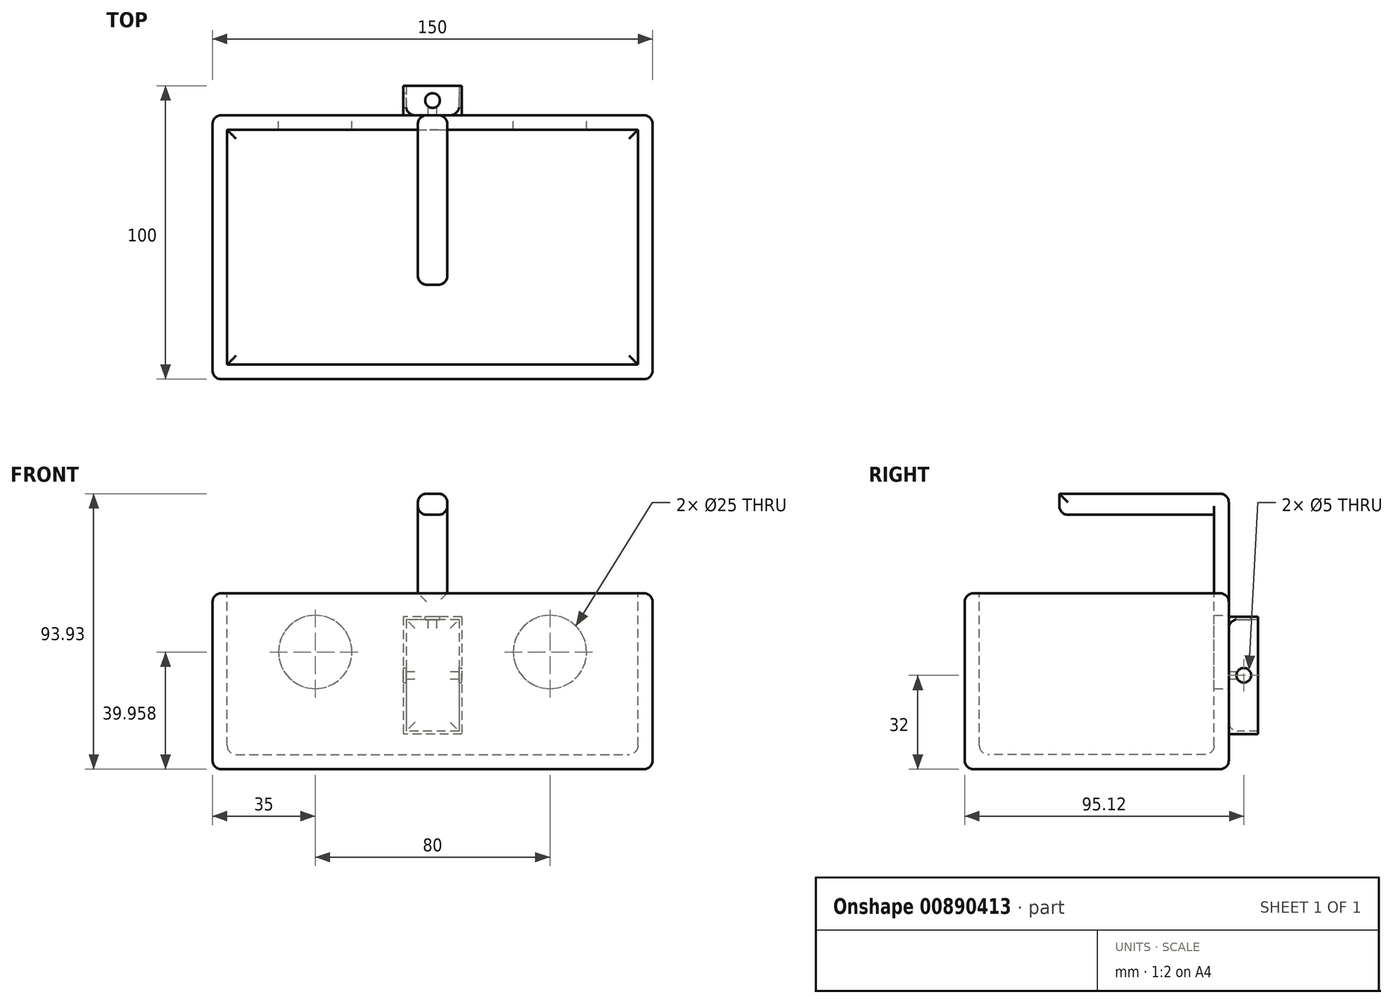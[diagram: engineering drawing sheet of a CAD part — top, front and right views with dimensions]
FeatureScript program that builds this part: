
annotation { "Feature Type Name" : "Feature", "Feature Type Description" : "" }
export const myFeature = defineFeature(function(context is Context, id is Id, definition is map)
    precondition{}
    {
        {
            var Q0;
            Q0=qCreatedBy(makeId("Top.planeOp"),FACE);
            var sketch = newSketch(context, id + "F0", { "sketchPlane" : qUnion([Q0])});
            skLineSegment(sketch, "E0.bottom", {"start": v(-75, 48.88) * mm, "end": v(75, 48.88) * mm});
            skLineSegment(sketch, "E0.top", {"start": v(-75, -41.12) * mm, "end": v(75, -41.12) * mm});
            skLineSegment(sketch, "E0.left", {"start": v(-75, 48.88) * mm, "end": v(-75, -41.12) * mm});
            skLineSegment(sketch, "E0.right", {"start": v(75, 48.88) * mm, "end": v(75, -41.12) * mm});
            skLineSegment(sketch, "E1.0", {"start": v(-69, 42.88) * mm, "end": v(69, 42.88) * mm});
            skLineSegment(sketch, "E1.1", {"start": v(-69, 42.88) * mm, "end": v(-69, -35.12) * mm});
            skLineSegment(sketch, "E1.2", {"start": v(-69, -35.12) * mm, "end": v(69, -35.12) * mm});
            skLineSegment(sketch, "E1.3", {"start": v(69, 42.88) * mm, "end": v(69, -35.12) * mm});
            skSolve(sketch);
        }
        {
            var Q0;
            Q0 = qSketchRegion(id + "F0", true);
            var Q1;
            Q1=makeQuery(id+"F0.imprint","IMPRINT",FACE,{"disambiguationData":[TD([[makeQuery(id+"F0.imprint","IMPRINT",EDGE,{"derivedFrom":sQuery(id+"F0.wireOp",EDGE,"E1.0")}),-1.0]])]});
            extrude(context, id + "F1", {"entities" : qUnion([Q0, Q1]), "depth" : 60 * mm, "offsetDistance" : 25 * mm});
        }
        {
            var Q0;
            Q0=makeQuery(id+"F1.opExtrude","CAP_FACE",FACE,{"disambiguationData":[OSD([sQuery(id+"F0.wireOp",EDGE,"E0.bottom"),sQuery(id+"F0.wireOp",EDGE,"E0.top"),sQuery(id+"F0.wireOp",EDGE,"E0.left"),sQuery(id+"F0.wireOp",EDGE,"E0.right")])],"isStart":false});
            var sketch = newSketch(context, id + "F2", { "sketchPlane" : qUnion([Q0])});
            skLineSegment(sketch, "E2.0", {"start": v(-70, 43.88) * mm, "end": v(70, 43.88) * mm});
            skLineSegment(sketch, "E2.1", {"start": v(-70, 43.88) * mm, "end": v(-70, -36.12) * mm});
            skLineSegment(sketch, "E2.2", {"start": v(-70, -36.12) * mm, "end": v(70, -36.12) * mm});
            skLineSegment(sketch, "E2.3", {"start": v(70, 43.88) * mm, "end": v(70, -36.12) * mm});
            skSolve(sketch);
        }
        {
            var Q0;
            Q0=makeQuery(id+"F2.imprint","IMPRINT",FACE,{"disambiguationData":[TD([[makeQuery(id+"F2.imprint","IMPRINT",EDGE,{"derivedFrom":sQuery(id+"F2.wireOp",EDGE,"E2.0")}),-1.0]])]});
            extrude(context, id + "F3", {"entities" : qUnion([Q0]), "operationType" : NewBodyOperationType.REMOVE, "oppositeDirection" : true, "depth" : 55 * mm, "offsetDistance" : 25 * mm});
        }
        {
            var Q0;
            Q0=makeQuery(id+"F1.opExtrude","SWEPT_FACE",FACE,{"disambiguationData":[OSD([sQuery(id+"F0.wireOp",EDGE,"E0.bottom")])]});
            var sketch = newSketch(context, id + "F4", { "sketchPlane" : qUnion([Q0])});
            skLineSegment(sketch, "E3", {"start": v(0, 79.82) * mm, "end": v(0, -42.25) * mm, "construction": true});
            skLineSegment(sketch, "E4", {"start": v(-86.25, 39.96) * mm, "end": v(125.43, 39.96) * mm, "construction": true});
            skCircle(sketch, "E5", {"center": v(-40, 39.96) * mm, "radius": 12.5 * mm});
            skCircle(sketch, "E6.1.0.0", {"center": v(40, 39.96) * mm, "radius": 12.5 * mm});
            skLineSegment(sketch, "E6.direction1", {"start": v(-40, 39.96) * mm, "end": v(40, 39.96) * mm, "construction": true});
            skSolve(sketch);
        }
        {
            var Q0;
            Q0 = qSketchRegion(id + "F4", true);
            extrude(context, id + "F5", {"entities" : qUnion([Q0]), "operationType" : NewBodyOperationType.REMOVE, "endBound" : BoundingType.UP_TO_NEXT, "oppositeDirection" : true, "depth" : 25 * mm, "offsetDistance" : 25 * mm});
        }
        {
            var Q0;
            Q0=makeQuery(id+"F1.opExtrude","SWEPT_FACE",FACE,{"disambiguationData":[OSD([sQuery(id+"F0.wireOp",EDGE,"E0.bottom")])]});
            var sketch = newSketch(context, id + "F6", { "sketchPlane" : qUnion([Q0])});
            skLineSegment(sketch, "E7", {"start": v(0, 78.55) * mm, "end": v(0, -36.33) * mm, "construction": true});
            skLineSegment(sketch, "E8.bottom", {"start": v(-10, 52) * mm, "end": v(10, 52) * mm});
            skLineSegment(sketch, "E8.top", {"start": v(-10, 12) * mm, "end": v(10, 12) * mm});
            skLineSegment(sketch, "E8.left", {"start": v(-10, 52) * mm, "end": v(-10, 12) * mm});
            skLineSegment(sketch, "E8.right", {"start": v(10, 52) * mm, "end": v(10, 12) * mm});
            skLineSegment(sketch, "E9.0", {"start": v(-9, 51) * mm, "end": v(-9, 13) * mm});
            skLineSegment(sketch, "E9.1", {"start": v(-9, 51) * mm, "end": v(9, 51) * mm});
            skLineSegment(sketch, "E9.2", {"start": v(9, 51) * mm, "end": v(9, 13) * mm});
            skLineSegment(sketch, "E9.3", {"start": v(-9, 13) * mm, "end": v(9, 13) * mm});
            skSolve(sketch);
        }
        {
            var Q0;
            Q0 = qSketchRegion(id + "F6", true);
            extrude(context, id + "F7", {"entities" : qUnion([Q0]), "operationType" : NewBodyOperationType.ADD, "depth" : 10 * mm, "offsetDistance" : 25 * mm});
        }
        {
            var Q0;
            Q0=makeQuery(id+"F7.opExtrude","SWEPT_FACE",FACE,{"disambiguationData":[OSD([sQuery(id+"F6.wireOp",EDGE,"E8.left")])]});
            var sketch = newSketch(context, id + "F8", { "sketchPlane" : qUnion([Q0])});
            skLineSegment(sketch, "E10", {"start": v(0, 77.28) * mm, "end": v(0, -8.98) * mm, "construction": true});
            skCircle(sketch, "E11", {"center": v(54, 32) * mm, "radius": 2.5 * mm});
            skSolve(sketch);
        }
        {
            var Q0;
            Q0 = qSketchRegion(id + "F8", true);
            extrude(context, id + "F9", {"entities" : qUnion([Q0]), "operationType" : NewBodyOperationType.REMOVE, "endBound" : BoundingType.THROUGH_ALL, "oppositeDirection" : true, "depth" : 25 * mm, "offsetDistance" : 25 * mm});
        }
        {
            var Q0;
            Q0=makeQuery(id+"F7.opExtrude","SWEPT_FACE",FACE,{"disambiguationData":[OSD([sQuery(id+"F6.wireOp",EDGE,"E8.bottom")])]});
            var sketch = newSketch(context, id + "F10", { "sketchPlane" : qUnion([Q0])});
            skCircle(sketch, "E12", {"center": v(0, 53.88) * mm, "radius": 2.5 * mm});
            skLineSegment(sketch, "E13", {"start": v(0, 62.32) * mm, "end": v(0, 34.94) * mm, "construction": true});
            skPoint(sketch, "E13.startSnap0", {"position": v(0, 58.88) * mm});
            skSolve(sketch);
        }
        {
            var Q0;
            Q0 = qSketchRegion(id + "F10", true);
            extrude(context, id + "F11", {"entities" : qUnion([Q0]), "operationType" : NewBodyOperationType.REMOVE, "endBound" : BoundingType.UP_TO_NEXT, "oppositeDirection" : true, "depth" : 25 * mm, "offsetDistance" : 25 * mm});
        }
        {
            var Q0;
            Q0 = qSketchRegion(id + "F8", true);
            extrude(context, id + "F12", {"entities" : qUnion([Q0]), "operationType" : NewBodyOperationType.REMOVE, "endBound" : BoundingType.THROUGH_ALL, "oppositeDirection" : true, "depth" : 25 * mm, "offsetDistance" : 25 * mm});
        }
        {
            var Q0;
            Q0=qCreatedBy(makeId("Right.planeOp"),FACE);
            var sketch = newSketch(context, id + "F13", { "sketchPlane" : qUnion([Q0])});
            skLineSegment(sketch, "E14.bottom", {"start": v(48.88, 60) * mm, "end": v(43.88, 60) * mm});
            skLineSegment(sketch, "E14.left", {"start": v(48.88, 60) * mm, "end": v(48.88, 93.93) * mm});
            skLineSegment(sketch, "E15.bottom", {"start": v(48.88, 93.93) * mm, "end": v(-8.9, 93.93) * mm});
            skLineSegment(sketch, "E15.top", {"start": v(43.88, 86.7) * mm, "end": v(-8.9, 86.7) * mm});
            skLineSegment(sketch, "E15.right", {"start": v(-8.9, 93.93) * mm, "end": v(-8.9, 86.7) * mm});
            skLineSegment(sketch, "E16", {"start": v(43.88, 86.7) * mm, "end": v(43.88, 60) * mm});
            skLineSegment(sketch, "E17", {"start": v(0, 0) * mm, "end": v(0, 83.82) * mm, "construction": true});
            skSolve(sketch);
        }
        {
            var Q0;
            Q0 = qSketchRegion(id + "F13", true);
            extrude(context, id + "F14", {"entities" : qUnion([Q0]), "operationType" : NewBodyOperationType.ADD, "depth" : 5 * mm, "offsetDistance" : 25 * mm, "hasSecondDirection" : true, "secondDirectionOppositeDirection" : true, "secondDirectionDepth" : 5 * mm});
        }
        {
            var Q0;
            Q0=makeQuery(id+"F1.opExtrude","SWEPT_FACE",FACE,{"disambiguationData":[OSD([sQuery(id+"F0.wireOp",EDGE,"E0.right")])]});
            var Q1;
            Q1=makeQuery(id+"F1.opExtrude","SWEPT_FACE",FACE,{"disambiguationData":[OSD([sQuery(id+"F0.wireOp",EDGE,"E0.top")])]});
            var Q2;
            Q2=makeQuery(id+"F1.opExtrude","CAP_FACE",FACE,{"disambiguationData":[OSD([sQuery(id+"F0.wireOp",EDGE,"E0.bottom"),sQuery(id+"F0.wireOp",EDGE,"E0.top"),sQuery(id+"F0.wireOp",EDGE,"E0.left"),sQuery(id+"F0.wireOp",EDGE,"E0.right")])],"isStart":true});
            var Q3;
            Q3=makeQuery(id+"F3.boolean.opBoolean","COPY",FACE,{"derivedFrom":makeQuery(id+"F3.opExtrude","CAP_FACE",FACE,{"disambiguationData":[OSD([sQuery(id+"F2.wireOp",EDGE,"E2.0"),sQuery(id+"F2.wireOp",EDGE,"E2.1"),sQuery(id+"F2.wireOp",EDGE,"E2.2"),sQuery(id+"F2.wireOp",EDGE,"E2.3")])],"isStart":false})});
            var Q4;
            Q4=makeQuery(id+"F1.opExtrude","SWEPT_FACE",FACE,{"disambiguationData":[OSD([sQuery(id+"F0.wireOp",EDGE,"E0.left")])]});
            var Q5;
            Q5=makeQuery(id+"F7.boolean.opBoolean","SPLIT",FACE,{"disambiguationData":[TD([makeQuery(id+"F7.opExtrude","SWEPT_FACE",FACE,{"disambiguationData":[OSD([sQuery(id+"F6.wireOp",EDGE,"E9.0")])]})])],"derivedFrom":makeQuery(id+"F1.opExtrude","SWEPT_FACE",FACE,{"disambiguationData":[OSD([sQuery(id+"F0.wireOp",EDGE,"E0.bottom")])]})});
            var Q6;
            Q6=makeQuery(id+"F14.opExtrude","CAP_EDGE",EDGE,{"disambiguationData":[OSD([sQuery(id+"F13.wireOp",EDGE,"E15.right")])],"isStart":true});
            var Q7;
            Q7=makeQuery(id+"F14.opExtrude","CAP_EDGE",EDGE,{"disambiguationData":[OSD([sQuery(id+"F13.wireOp",EDGE,"E15.top")])],"isStart":true});
            var Q8;
            Q8=makeQuery(id+"F14.opExtrude","CAP_EDGE",EDGE,{"disambiguationData":[OSD([sQuery(id+"F13.wireOp",EDGE,"E15.top")])],"isStart":false});
            var Q9;
            Q9=makeQuery(id+"F14.opExtrude","CAP_EDGE",EDGE,{"disambiguationData":[OSD([sQuery(id+"F13.wireOp",EDGE,"E15.right")])],"isStart":false});
            var Q10;
            Q10=makeQuery(id+"F14.opExtrude","SWEPT_EDGE",EDGE,{"disambiguationData":[OSD([sQuery(id+"F13.wireOp",EDGE,"E15.top"),sQuery(id+"F13.wireOp",EDGE,"E15.right")])]});
            var Q11;
            Q11=makeQuery(id+"F14.opExtrude","CAP_EDGE",EDGE,{"disambiguationData":[OSD([sQuery(id+"F13.wireOp",EDGE,"E15.bottom")])],"isStart":true});
            var Q12;
            Q12=makeQuery(id+"F14.opExtrude","CAP_EDGE",EDGE,{"disambiguationData":[OSD([sQuery(id+"F13.wireOp",EDGE,"E15.bottom")])],"isStart":false});
            fillet(context, id + "F15", {"entities" : qUnion([Q0, Q1, Q2, Q3, Q4, Q5, Q6, Q7, Q8, Q9, Q10, Q11, Q12]), "radius" : 3 * mm, "tangentPropagation" : true, "allowEdgeOverflow" : false});
        }
        {
            var Q0;
            {var subQ1=sQuery(id+"F0.wireOp",EDGE,"E0.right");var subQ2=sQuery(id+"F0.wireOp",EDGE,"E0.bottom");Q0=makeQuery(id+"F14.boolean.opBoolean","SPLIT",EDGE,{"disambiguationData":[TD([makeQuery(id+"F1.opExtrude","SWEPT_FACE",FACE,{"disambiguationData":[OSD([subQ1])]})])],"derivedFrom":makeQuery(id+"F1.opExtrude","CAP_EDGE",EDGE,{"disambiguationData":[OSD([subQ2])],"isStart":false})});}
            var Q1;
            Q1=makeQuery(id+"F14.opExtrude","CAP_EDGE",EDGE,{"disambiguationData":[OSD([sQuery(id+"F13.wireOp",EDGE,"E14.left")])],"isStart":false});
            var Q2;
            {var subQ1=sQuery(id+"F0.wireOp",EDGE,"E0.bottom");var subQ2=sQuery(id+"F0.wireOp",EDGE,"E0.left");Q2=makeQuery(id+"F14.boolean.opBoolean","SPLIT",EDGE,{"disambiguationData":[TD([makeQuery(id+"F1.opExtrude","SWEPT_FACE",FACE,{"disambiguationData":[OSD([subQ2])]})])],"derivedFrom":makeQuery(id+"F1.opExtrude","CAP_EDGE",EDGE,{"disambiguationData":[OSD([subQ1])],"isStart":false})});}
            var Q3;
            Q3=makeQuery(id+"F7.opExtrude","CAP_EDGE",EDGE,{"disambiguationData":[OSD([sQuery(id+"F6.wireOp",EDGE,"E8.left")])],"isStart":true});
            var Q4;
            Q4=makeQuery(id+"F7.opExtrude","CAP_EDGE",EDGE,{"disambiguationData":[OSD([sQuery(id+"F6.wireOp",EDGE,"E8.top")])],"isStart":true});
            var Q5;
            Q5=makeQuery(id+"F7.opExtrude","CAP_EDGE",EDGE,{"disambiguationData":[OSD([sQuery(id+"F6.wireOp",EDGE,"E8.right")])],"isStart":true});
            var Q6;
            Q6=makeQuery(id+"F7.opExtrude","CAP_EDGE",EDGE,{"disambiguationData":[OSD([sQuery(id+"F6.wireOp",EDGE,"E8.bottom")])],"isStart":true});
            fillet(context, id + "F16", {"entities" : qUnion([Q0, Q1, Q2, Q3, Q4, Q5, Q6]), "radius" : 3 * mm, "tangentPropagation" : true, "allowEdgeOverflow" : false});
        }
    });
